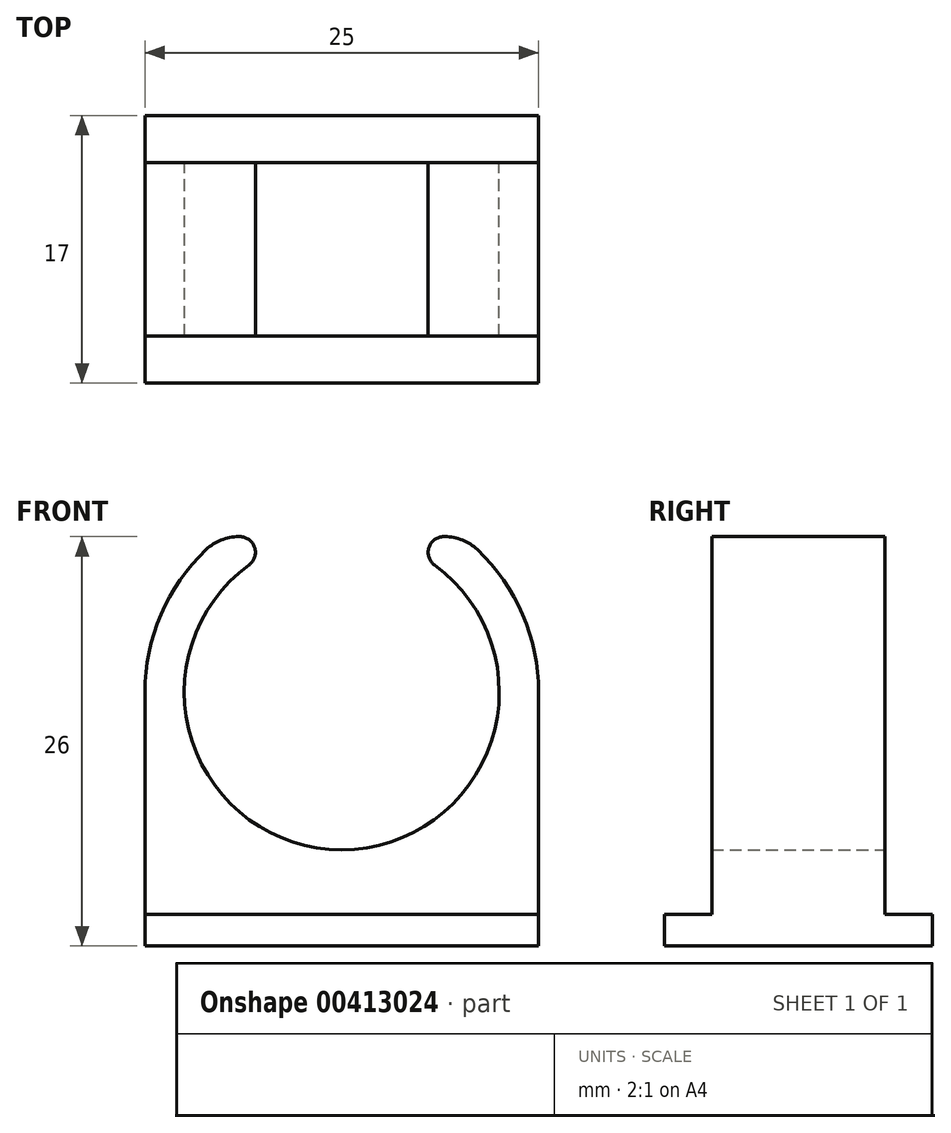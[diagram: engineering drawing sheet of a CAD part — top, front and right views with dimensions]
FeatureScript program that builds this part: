
annotation { "Feature Type Name" : "Feature", "Feature Type Description" : "" }
export const myFeature = defineFeature(function(context is Context, id is Id, definition is map)
    precondition{}
    {
        {
            var Q0;
            Q0=qCreatedBy(makeId("Front.planeOp"),FACE);
            var sketch = newSketch(context, id + "F0", { "sketchPlane" : qUnion([Q0])});
            skLineSegment(sketch, "E0.bottom", {"start": v(0, 0) * mm, "end": v(25, 0) * mm});
            skLineSegment(sketch, "E0.top", {"start": v(5.95, 24) * mm, "end": v(6.01, 24) * mm});
            skLineSegment(sketch, "E0.left", {"start": v(0, 0) * mm, "end": v(0, 14.12) * mm});
            skLineSegment(sketch, "E0.right", {"start": v(25, 0) * mm, "end": v(25, 14.12) * mm});
            skArc(sketch, "E1", {"start": v(6.6, 22.2) * mm, "mid": v(12.5, 4.12) * mm, "end": v(18.4, 22.2) * mm});
            skPoint(sketch, "E1.centerSnap0", {"position": v(12.5, 24) * mm});
            skArc(sketch, "E2", {"start": v(3.88, 23.17) * mm, "mid": v(1.01, 19.04) * mm, "end": v(0, 14.12) * mm});
            skArc(sketch, "E3.trimOffspring", {"start": v(25, 14.12) * mm, "mid": v(23.99, 19.04) * mm, "end": v(21.12, 23.17) * mm});
            skPoint(sketch, "E4.orphan", {"position": v(0, 24) * mm});
            skLineSegment(sketch, "E5.trimOffspring", {"start": v(18.99, 24) * mm, "end": v(19.05, 24) * mm});
            skPoint(sketch, "E6.orphan", {"position": v(25, 24) * mm});
            skPoint(sketch, "E7.visualSharp", {"position": v(10.97, 24) * mm});
            skArc(sketch, "E7.filletArc", {"start": v(6.6, 22.2) * mm, "mid": v(6.96, 23.31) * mm, "end": v(6.01, 24) * mm});
            skPoint(sketch, "E8.visualSharp", {"position": v(14.03, 24) * mm});
            skArc(sketch, "E8.filletArc", {"start": v(18.99, 24) * mm, "mid": v(18.04, 23.31) * mm, "end": v(18.4, 22.2) * mm});
            skPoint(sketch, "E9.visualSharp", {"position": v(4.85, 24) * mm});
            skArc(sketch, "E9.filletArc", {"start": v(5.95, 24) * mm, "mid": v(4.84, 23.79) * mm, "end": v(3.88, 23.17) * mm});
            skPoint(sketch, "E10.visualSharp", {"position": v(20.15, 24) * mm});
            skArc(sketch, "E10.filletArc", {"start": v(21.12, 23.17) * mm, "mid": v(20.16, 23.79) * mm, "end": v(19.05, 24) * mm});
            skSolve(sketch);
        }
        {
            var Q0;
            Q0=qSketchRegion(id+"F0",true);
            extrude(context, id + "F1", {"entities" : qUnion([Q0]), "depth" : 11 * mm});
        }
        {
            var Q0;
            Q0=makeQuery(id+"F1.opExtrude","SWEPT_FACE",FACE,{"disambiguationData":[OSD([sQuery(id+"F0.wireOp",EDGE,"E0.bottom")])]});
            var sketch = newSketch(context, id + "F2", { "sketchPlane" : qUnion([Q0])});
            skLineSegment(sketch, "E11.bottom", {"start": v(0, 14) * mm, "end": v(25, 14) * mm});
            skLineSegment(sketch, "E11.top", {"start": v(0, -3) * mm, "end": v(25, -3) * mm});
            skLineSegment(sketch, "E11.left", {"start": v(0, 14) * mm, "end": v(0, -3) * mm});
            skLineSegment(sketch, "E11.right", {"start": v(25, 14) * mm, "end": v(25, -3) * mm});
            skSolve(sketch);
        }
        {
            var Q0;
            Q0=qSketchRegion(id+"F2",true);
            extrude(context, id + "F3", {"entities" : qUnion([Q0]), "operationType" : NewBodyOperationType.ADD, "depth" : 2 * mm});
        }
    });
